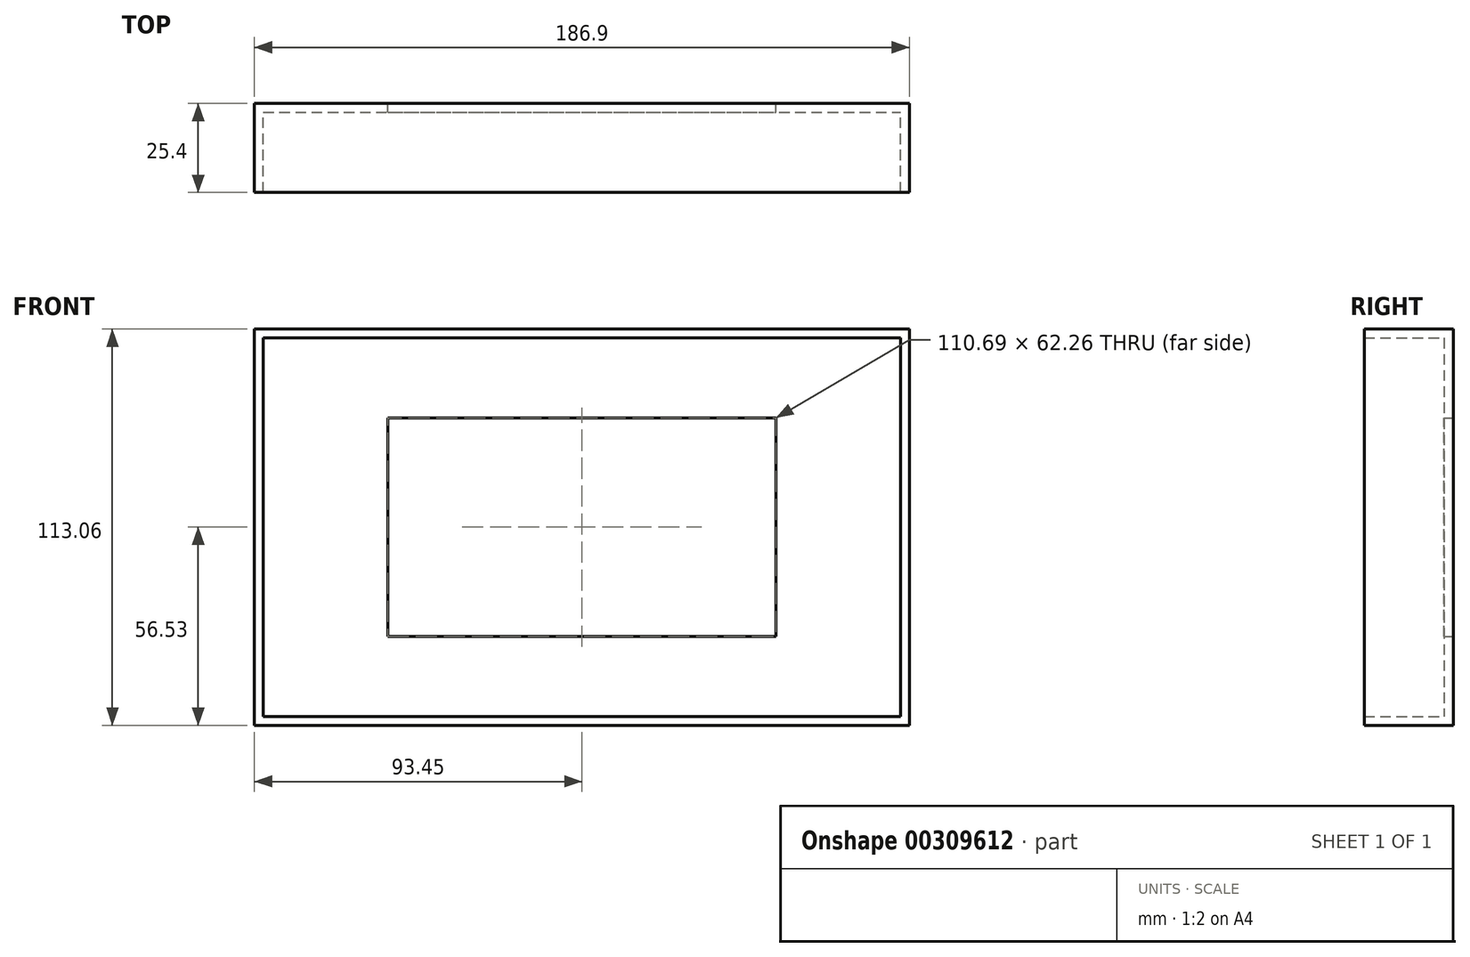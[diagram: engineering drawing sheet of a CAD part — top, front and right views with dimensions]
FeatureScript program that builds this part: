
annotation { "Feature Type Name" : "Feature", "Feature Type Description" : "" }
export const myFeature = defineFeature(function(context is Context, id is Id, definition is map)
    precondition{}
    {
        {
            var Q0;
            Q0=qCreatedBy(makeId("Front.planeOp"),FACE);
            var sketch = newSketch(context, id + "F0", { "sketchPlane" : qUnion([Q0])});
            skLineSegment(sketch, "E0.bottom", {"start": v(55.35, 31.13) * mm, "end": v(-55.35, 31.13) * mm});
            skLineSegment(sketch, "E0.top", {"start": v(55.35, -31.13) * mm, "end": v(-55.35, -31.13) * mm});
            skLineSegment(sketch, "E0.left", {"start": v(55.35, 31.13) * mm, "end": v(55.35, -31.13) * mm});
            skLineSegment(sketch, "E0.right", {"start": v(-55.35, 31.13) * mm, "end": v(-55.35, -31.13) * mm});
            skPoint(sketch, "E0.middle", {"position": v(0, 0) * mm});
            skSolve(sketch);
        }
        {
            var Q0;
            Q0=qCreatedBy(makeId("Front.planeOp"),FACE);
            var sketch = newSketch(context, id + "F1", { "sketchPlane" : qUnion([Q0])});
            skLineSegment(sketch, "E1", {"start": v(-93.45, 56.53) * mm, "end": v(-93.45, -56.53) * mm});
            skLineSegment(sketch, "E2", {"start": v(-93.45, 56.53) * mm, "end": v(93.45, 56.53) * mm});
            skLineSegment(sketch, "E3", {"start": v(93.45, 56.53) * mm, "end": v(93.45, -56.53) * mm});
            skLineSegment(sketch, "E4", {"start": v(-93.45, -56.53) * mm, "end": v(93.45, -56.53) * mm});
            skSolve(sketch);
        }
        {
            var Q0;
            Q0=makeQuery(id+"F1.imprint","IMPRINT",FACE,{"disambiguationData":[TD([[makeQuery(id+"F1.imprint","IMPRINT",EDGE,{"derivedFrom":sQuery(id+"F1.wireOp",EDGE,"E1")}),1.0]])]});
            extrude(context, id + "F2", {"entities" : qUnion([Q0]), "depth" : 25.4 * mm});
        }
        {
            var Q0;
            Q0=makeQuery(id+"F2.opExtrude","CAP_FACE",FACE,{"disambiguationData":[OSD([sQuery(id+"F1.wireOp",EDGE,"E1"),sQuery(id+"F1.wireOp",EDGE,"E2"),sQuery(id+"F1.wireOp",EDGE,"E3"),sQuery(id+"F1.wireOp",EDGE,"E4")])],"isStart":false});
            shell(context, id + "F3", {"entities" : qUnion([Q0]), "thickness" : 2.54 * mm});
        }
        {
            var Q0;
            Q0=makeQuery(id+"F0.imprint","IMPRINT",FACE,{"disambiguationData":[TD([[makeQuery(id+"F0.imprint","IMPRINT",EDGE,{"derivedFrom":sQuery(id+"F0.wireOp",EDGE,"E0.bottom")}),1.0]])]});
            extrude(context, id + "F4", {"entities" : qUnion([Q0]), "operationType" : NewBodyOperationType.REMOVE, "endBound" : BoundingType.THROUGH_ALL, "depth" : 25.4 * mm});
        }
    });
